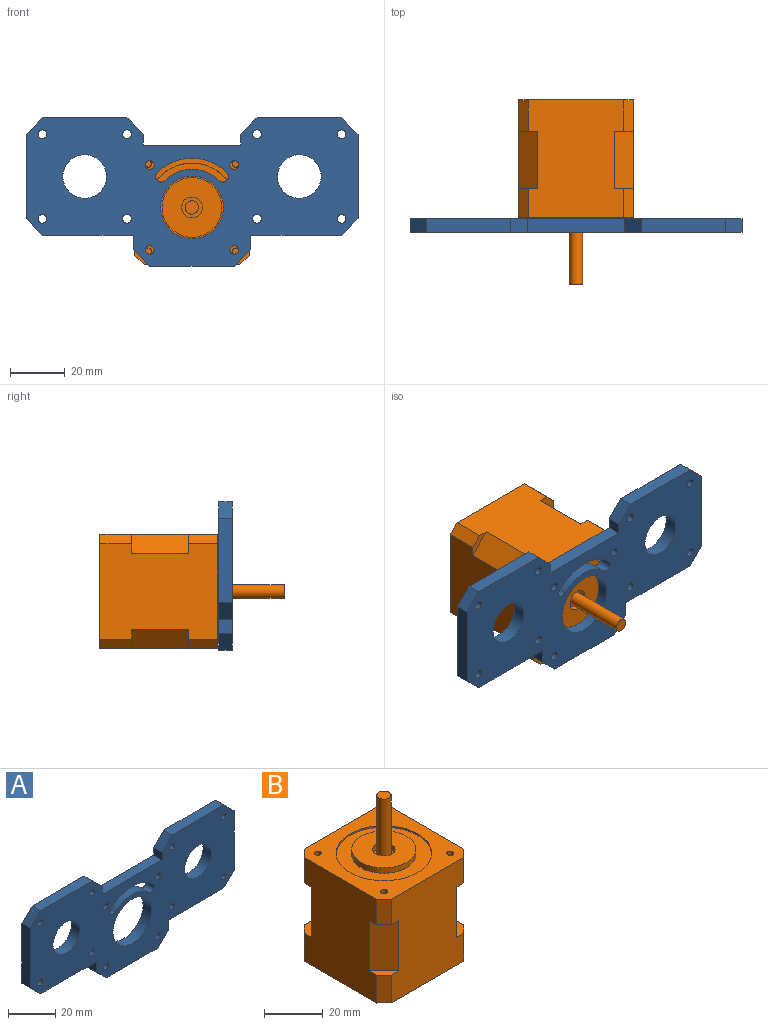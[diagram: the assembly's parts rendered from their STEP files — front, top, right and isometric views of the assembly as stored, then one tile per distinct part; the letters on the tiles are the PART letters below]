
ASSEMBLY  parts=2 mates=1
PART A: 41 faces, bbox 121.6x5x54.3 mm
  f0: cylinder r=2mm len=5mm, axis (0,1,0), area 31.4mm2, adj f1,f24,f39,f40
  f1: cylinder r=14mm len=19.8mm, axis (0,1,0), area 110mm2, adj f0,f2,f39,f40
  f2: cylinder r=2mm len=5mm, axis (0,1,0), area 31.4mm2, adj f1,f24,f39,f40
  f3: plane 5x4mm, normal (-1,0,0), area 20mm2, adj f4,f37,f39,f40
  f4: plane 35.63x5mm, normal (0,0,1), area 178.1mm2, adj f3,f5,f39,f40
  f5: plane 5x4mm, normal (1,0,0), area 20mm2, adj f4,f6,f39,f40
  f6: plane 6x6mm, normal (0.71,0,0.71), area 42.4mm2, adj f5,f7,f39,f40
  f7: plane 31x5mm, normal (0,0,1), area 155mm2, adj f6,f8,f39,f40
  f8: plane 6x6mm, normal (-0.71,0,0.71), area 42.4mm2, adj f7,f9,f39,f40
  f9: plane 31x5mm, normal (-1,0,0), area 155mm2, adj f8,f10,f39,f40
  f10: plane 6x6mm, normal (-0.71,0,-0.71), area 42.4mm2, adj f9,f11,f39,f40
  f11: plane 33.31x5mm, normal (0,0,-1), area 166.6mm2, adj f10,f12,f39,f40
  f12: plane 5.31x5mm, normal (-1,0,0), area 26.6mm2, adj f11,f13,f39,f40
  f13: plane 6x6mm, normal (-0.71,0,-0.71), area 42.4mm2, adj f12,f14,f39,f40
  f14: plane 31x5mm, normal (0,0,-1), area 155mm2, adj f13,f15,f39,f40
  f15: plane 6x6mm, normal (0.71,0,-0.71), area 42.4mm2, adj f14,f16,f39,f40
  f16: plane 5.31x5mm, normal (1,0,0), area 26.6mm2, adj f15,f17,f39,f40
  f17: plane 33.31x5mm, normal (0,0,-1), area 166.6mm2, adj f16,f18,f39,f40
  f18: plane 6x6mm, normal (0.71,0,-0.71), area 42.4mm2, adj f17,f19,f39,f40
  f19: plane 31x5mm, normal (1,0,0), area 155mm2, adj f18,f20,f39,f40
  f20: plane 6x6mm, normal (0.71,0,0.71), area 42.4mm2, adj f19,f21,f39,f40
  f21: plane 31x5mm, normal (0,0,1), area 155mm2, adj f20,f37,f39,f40
  f22: cylinder r=8mm len=16mm, axis (0,1,0), area 251.3mm2, adj f39,f40
  f23: cylinder r=8mm len=16mm, axis (0,1,0), area 251.3mm2, adj f39,f40
  f24: cylinder r=18mm len=25.46mm, axis (0,1,0), area 141.4mm2, adj f0,f2,f39,f40
  f25: cylinder r=1.6mm len=5mm, axis (0,1,0), area 50.3mm2, adj f39,f40
  f26: cylinder r=1.6mm len=5mm, axis (0,1,0), area 50.3mm2, adj f39,f40
  f27: cylinder r=1.6mm len=5mm, axis (0,1,0), area 50.3mm2, adj f39,f40
  f28: cylinder r=1.6mm len=5mm, axis (0,1,0), area 50.3mm2, adj f39,f40
  f29: cylinder r=1.6mm len=5mm, axis (0,1,0), area 50.3mm2, adj f39,f40
  f30: cylinder r=1.6mm len=5mm, axis (0,1,0), area 50.3mm2, adj f39,f40
  f31: cylinder r=1.6mm len=5mm, axis (0,1,0), area 50.3mm2, adj f39,f40
  f32: cylinder r=1.6mm len=5mm, axis (0,1,0), area 50.3mm2, adj f39,f40
  f33: cylinder r=11.5mm len=23mm, axis (0,1,0), area 361.3mm2, adj f39,f40
  f34: cylinder r=1.6mm len=5mm, axis (0,1,0), area 50.3mm2, adj f39,f40
  f35: cylinder r=1.6mm len=5mm, axis (0,1,0), area 50.3mm2, adj f39,f40
  f36: cylinder r=1.6mm len=5mm, axis (0,1,0), area 50.3mm2, adj f39,f40
  f37: plane 6x6mm, normal (-0.71,0,0.71), area 42.4mm2, adj f3,f21,f39,f40
  f38: cylinder r=1.6mm len=5mm, axis (0,1,0), area 50.3mm2, adj f39,f40
  f39: plane 121.63x54.31mm, normal (0,-1,0), area 4189mm2, adj f0,f1,f2,f3,f4,f5,f6,f7
  f40: plane 121.63x54.31mm, normal (0,1,0), area 4189mm2, adj f0,f1,f2,f3,f4,f5,f6,f7
PART B: 42 faces, bbox 42x42x67.6 mm
  f0: plane 11.65x3.54mm, normal (-0.71,0.71,0), area 58.2mm2, adj f4,f6,f7,f16
  f1: plane 11.65x3.54mm, normal (0.71,0.71,0), area 58.2mm2, adj f4,f7,f10,f25
  f2: plane 11.65x3.54mm, normal (0.71,-0.71,0), area 58.2mm2, adj f5,f7,f10,f22
  f3: plane 10.65x3.54mm, normal (-0.71,-0.71,0), area 53.2mm2, adj f5,f6,f13,f17
  f4: plane 43.3x34.93mm, normal (0,1,0), area 1363.9mm2, adj f0,f1,f7,f8,f9,f13,f14,f15
  f5: plane 43.3x34.93mm, normal (0,-1,0), area 1363.9mm2, adj f2,f3,f7,f11,f12,f13,f17,f18
  f6: plane 43.3x34.93mm, normal (-1,0,0), area 1363.9mm2, adj f0,f3,f7,f8,f12,f13,f14,f15
  f7: plane 42x42mm, normal (0,0,-1), area 1739mm2, adj f0,f1,f2,f4,f5,f6,f10,f12
  f8: plane 10.65x3.54mm, normal (-0.71,0.71,0), area 53.2mm2, adj f4,f6,f13,f14
  f9: plane 10.65x3.54mm, normal (0.71,0.71,0), area 53.2mm2, adj f4,f10,f13,f23
  f10: plane 43.3x34.93mm, normal (1,0,0), area 1363.9mm2, adj f1,f2,f7,f9,f11,f13,f20,f21
  f11: plane 10.65x3.54mm, normal (0.71,-0.71,0), area 53.2mm2, adj f5,f10,f13,f20
  f12: plane 11.65x3.54mm, normal (-0.71,-0.71,0), area 58.2mm2, adj f5,f6,f7,f18
  f13: plane 42x42mm, normal (0,0,1), area 888.7mm2, adj f3,f4,f5,f6,f8,f9,f10,f11
  f14: plane 7.07x7.07mm, normal (0,0,-1), area 18.8mm2, adj f4,f6,f8,f15
  f15: plane 21x7.07mm, normal (-0.71,0.71,0), area 210mm2, adj f4,f6,f14,f16
  f16: plane 7.07x7.07mm, normal (0,0,1), area 18.8mm2, adj f0,f4,f6,f15
  f17: plane 7.07x7.07mm, normal (0,0,-1), area 18.8mm2, adj f3,f5,f6,f19
  f18: plane 7.07x7.07mm, normal (0,0,1), area 18.8mm2, adj f5,f6,f12,f19
  f19: plane 21x7.07mm, normal (-0.71,-0.71,0), area 210mm2, adj f5,f6,f17,f18
  f20: plane 7.07x7.07mm, normal (0,0,-1), area 18.8mm2, adj f5,f10,f11,f21
  f21: plane 21x7.07mm, normal (0.71,-0.71,0), area 210mm2, adj f5,f10,f20,f22
  f22: plane 7.07x7.07mm, normal (0,0,1), area 18.8mm2, adj f2,f5,f10,f21
  f23: plane 7.07x7.07mm, normal (0,0,-1), area 18.8mm2, adj f4,f9,f10,f24
  f24: plane 21x7.07mm, normal (0.71,0.71,0), area 210mm2, adj f4,f10,f23,f25
  f25: plane 7.07x7.07mm, normal (0,0,1), area 18.8mm2, adj f1,f4,f10,f24
  f26: plane 2.4x2.4mm, normal (0,0,1), area 4.5mm2, adj f27
  f27: cylinder r=1.2mm len=5mm, axis (0,0,1), area 37.7mm2, adj f13,f26
  f28: plane 2.4x2.4mm, normal (0,0,1), area 4.5mm2, adj f29
  f29: cylinder r=1.2mm len=5mm, axis (0,0,1), area 37.7mm2, adj f13,f28
  f30: plane 2.4x2.4mm, normal (0,0,1), area 4.5mm2, adj f31
  f31: cylinder r=1.2mm len=5mm, axis (0,0,1), area 37.7mm2, adj f13,f30
  f32: plane 2.4x2.4mm, normal (0,0,1), area 4.5mm2, adj f33
  f33: cylinder r=1.2mm len=5mm, axis (0,0,1), area 37.7mm2, adj f13,f32
  f34: cylinder r=16.28mm len=32.55mm, axis (0,0,1), area 66.5mm2, adj f13,f35
  f35: plane 32.55x32.55mm, normal (0,0,1), area 455.5mm2, adj f34,f36
  f36: cylinder r=10.95mm len=21.9mm, axis (0,0,1), area 154.8mm2, adj f35,f37
  f37: plane 21.9x21.9mm, normal (0,0,1), area 330.8mm2, adj f36,f40
  f38: cylinder r=2.44mm len=24.9mm, axis (0,0,1), area 381.3mm2, adj f39,f41
  f39: plane 7.65x7.65mm, normal (0,0,1), area 27.3mm2, adj f38,f40
  f40: cylinder r=3.83mm len=7.65mm, axis (0,0,1), area 54.1mm2, adj f37,f39
  f41: plane 4.88x4.88mm, normal (0,0,1), area 18.7mm2, adj f38
PLACE A t=(4.01,-37.75,3.08)mm
PLACE B rot(axis=(1,0,0),90deg) t=(0,-39.1,3.03)mm
MATE planar A.f33 <-> B.f34  axis (0,-1,0) through (4.01,-42.75,3.08)mm
